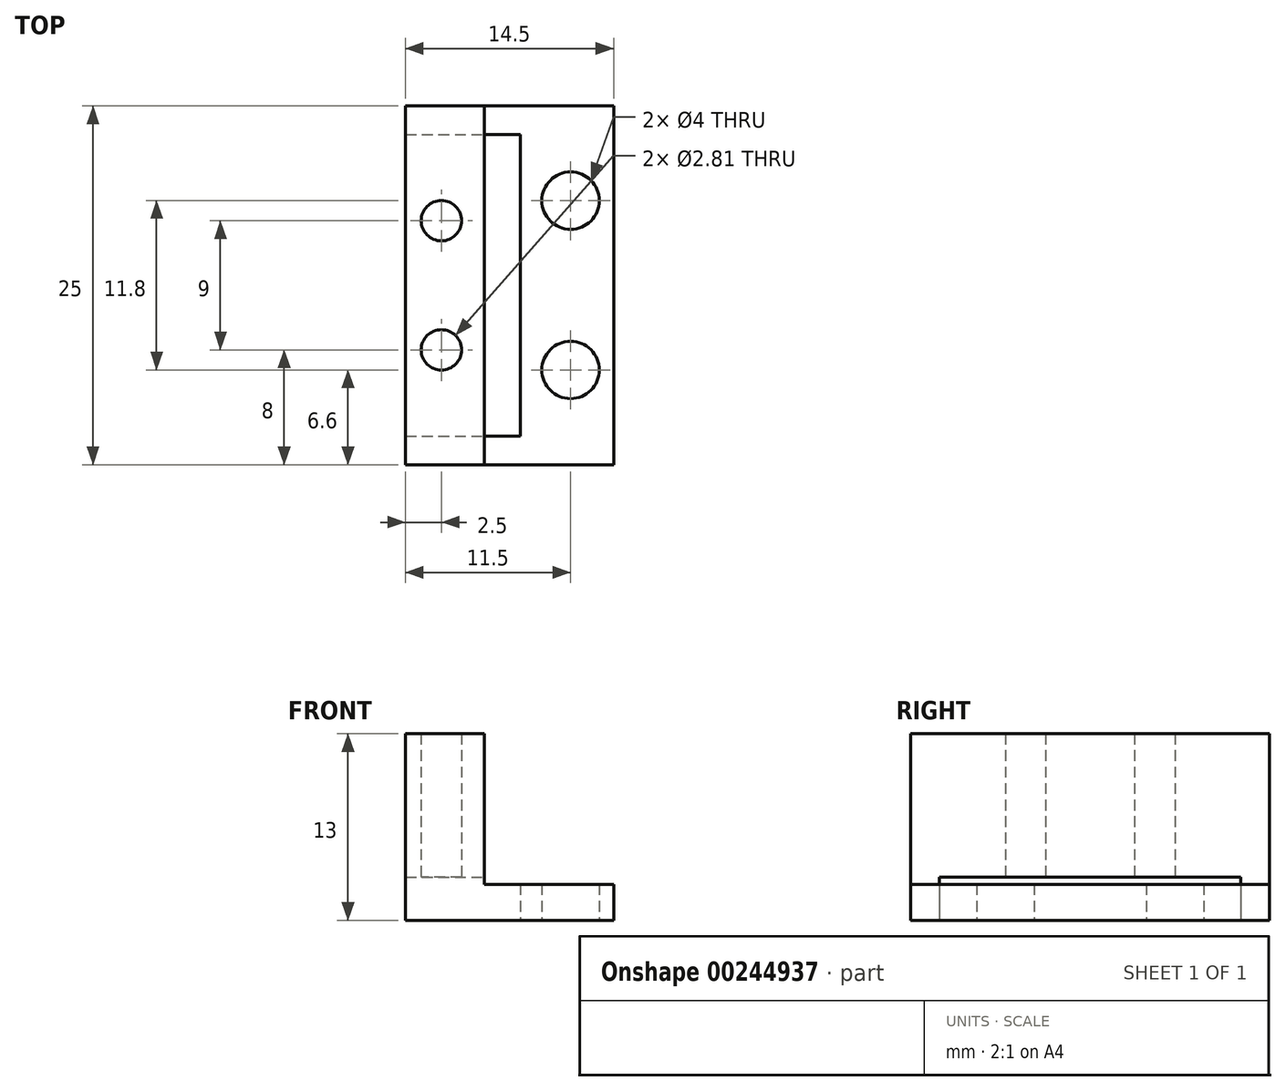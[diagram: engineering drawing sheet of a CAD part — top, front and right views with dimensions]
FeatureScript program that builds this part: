
annotation { "Feature Type Name" : "Feature", "Feature Type Description" : "" }
export const myFeature = defineFeature(function(context is Context, id is Id, definition is map)
    precondition{}
    {
        {
            var Q0;
            Q0=qCreatedBy(makeId("Top.planeOp"),FACE);
            var sketch = newSketch(context, id + "F0", { "sketchPlane" : qUnion([Q0])});
            skLineSegment(sketch, "E0", {"start": v(0, 0) * mm, "end": v(26, 0) * mm});
            skLineSegment(sketch, "E1.bottom", {"start": v(26, 0) * mm, "end": v(36.5, 0) * mm});
            skLineSegment(sketch, "E1.top", {"start": v(26, 25) * mm, "end": v(36.5, 25) * mm});
            skLineSegment(sketch, "E1.left", {"start": v(26, 0) * mm, "end": v(26, 25) * mm});
            skLineSegment(sketch, "E1.right", {"start": v(36.5, 0) * mm, "end": v(36.5, 25) * mm});
            skLineSegment(sketch, "E2", {"start": v(26, 12.5) * mm, "end": v(33.5, 12.5) * mm});
            skLineSegment(sketch, "E3", {"start": v(33.5, 12.5) * mm, "end": v(33.5, 18.4) * mm});
            skCircle(sketch, "E4", {"center": v(33.5, 18.4) * mm, "radius": 2 * mm});
            skCircle(sketch, "E5.MirrorC", {"center": v(33.5, 6.6) * mm, "radius": 2 * mm});
            skSolve(sketch);
        }
        {
            var Q0;
            Q0 = qSketchRegion(id + "F0", true);
            extrude(context, id + "F1", {"entities" : qUnion([Q0]), "depth" : 2.5 * mm});
        }
        {
            var Q0;
            Q0=qCreatedBy(makeId("Top.planeOp"),FACE);
            var sketch = newSketch(context, id + "F2", { "sketchPlane" : qUnion([Q0])});
            skLineSegment(sketch, "E6", {"start": v(0, 0) * mm, "end": v(22, 0) * mm});
            skLineSegment(sketch, "E7.bottom", {"start": v(22, 0) * mm, "end": v(27.5, 0) * mm});
            skLineSegment(sketch, "E7.top", {"start": v(22, 25) * mm, "end": v(27.5, 25) * mm});
            skLineSegment(sketch, "E7.left", {"start": v(22, 0) * mm, "end": v(22, 25) * mm});
            skLineSegment(sketch, "E7.right", {"start": v(27.5, 0) * mm, "end": v(27.5, 25) * mm});
            skLineSegment(sketch, "E8", {"start": v(22, 12.5) * mm, "end": v(24.5, 12.5) * mm});
            skLineSegment(sketch, "E9", {"start": v(24.5, 12.5) * mm, "end": v(24.5, 17) * mm});
            skCircle(sketch, "E10", {"center": v(24.5, 17) * mm, "radius": 1.4 * mm});
            skCircle(sketch, "E11.MirrorC", {"center": v(24.5, 8) * mm, "radius": 1.4 * mm});
            skSolve(sketch);
        }
        {
            var Q0;
            Q0 = qSketchRegion(id + "F2", true);
            extrude(context, id + "F3", {"entities" : qUnion([Q0]), "operationType" : NewBodyOperationType.ADD, "depth" : 13 * mm});
        }
        {
            var Q0;
            Q0=qCreatedBy(makeId("Top.planeOp"),FACE);
            var sketch = newSketch(context, id + "F4", { "sketchPlane" : qUnion([Q0])});
            skLineSegment(sketch, "E12", {"start": v(0, 0) * mm, "end": v(21.5, 0) * mm});
            skLineSegment(sketch, "E13", {"start": v(21.5, 0) * mm, "end": v(21.5, 2) * mm});
            skLineSegment(sketch, "E14.bottom", {"start": v(21.5, 2) * mm, "end": v(30, 2) * mm});
            skLineSegment(sketch, "E14.top", {"start": v(21.5, 23) * mm, "end": v(30, 23) * mm});
            skLineSegment(sketch, "E14.left", {"start": v(21.5, 2) * mm, "end": v(21.5, 23) * mm});
            skLineSegment(sketch, "E14.right", {"start": v(30, 2) * mm, "end": v(30, 23) * mm});
            skSolve(sketch);
        }
        {
            var Q0;
            Q0 = qSketchRegion(id + "F4", true);
            extrude(context, id + "F5", {"entities" : qUnion([Q0]), "operationType" : NewBodyOperationType.REMOVE, "depth" : 3 * mm});
        }
    });
